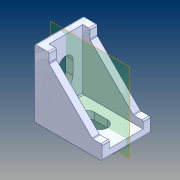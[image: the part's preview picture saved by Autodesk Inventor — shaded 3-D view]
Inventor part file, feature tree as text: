
AUTODESK INVENTOR PART (.ipt)
format: ipt  version: 2021 (Build 250183000, 183)  size: 161,792 bytes
history: native  units: mm
features: fillet x1
ambient origin geometry x8: Origin, YZ Plane, XZ Plane, XY Plane, X Axis, Y Axis, Z Axis, Center Point
bodies: Solid1 (feature_tree)
feature tree (1):
  fillet  "Fillet5"  [1 undecoded]
note: 1 required parameter value undecoded (feature->parameter linkage not recoverable at this tier; creation-order binding heuristic only, values carry confidence <= 0.55)
